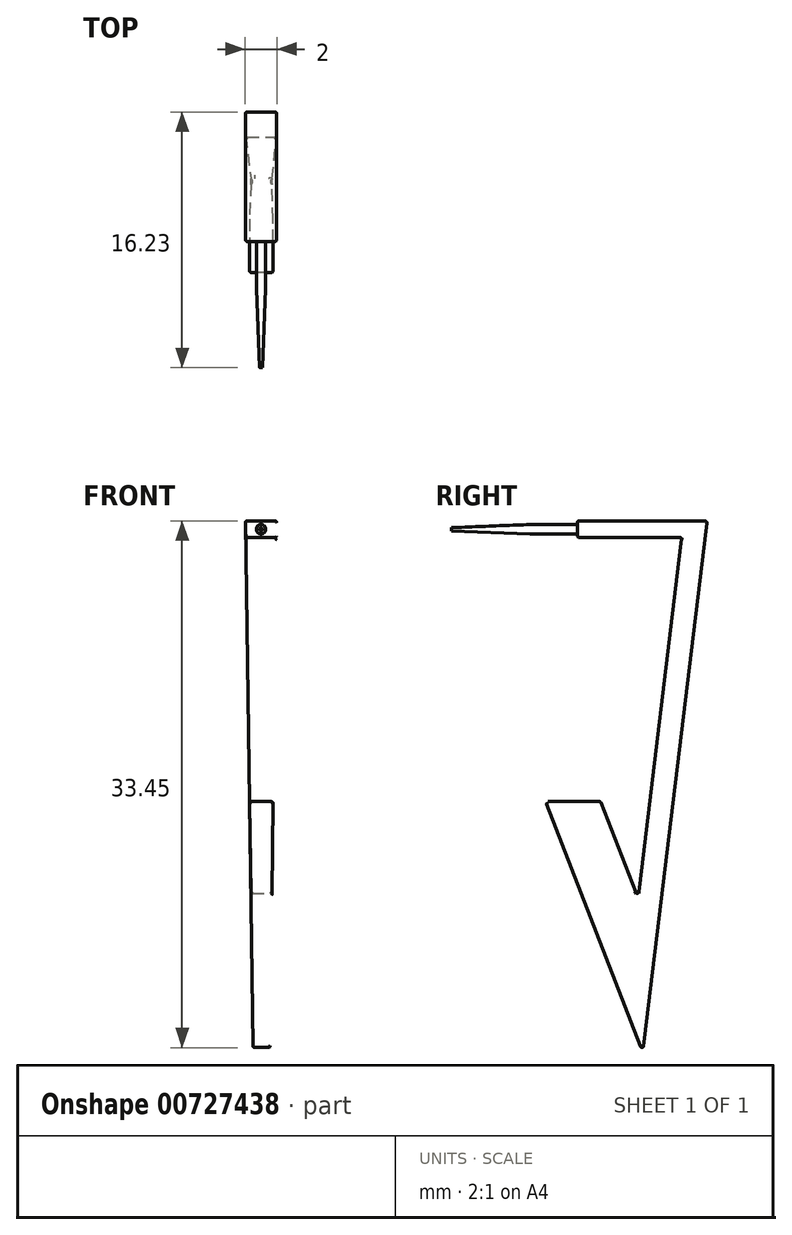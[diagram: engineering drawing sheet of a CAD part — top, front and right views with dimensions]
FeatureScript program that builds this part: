
annotation { "Feature Type Name" : "Feature", "Feature Type Description" : "" }
export const myFeature = defineFeature(function(context is Context, id is Id, definition is map)
    precondition{}
    {
        {
            var Q0;
            Q0=qCreatedBy(makeId("Right.planeOp"),FACE);
            var sketch = newSketch(context, id + "F0", { "sketchPlane" : qUnion([Q0])});
            skLineSegment(sketch, "E0", {"start": v(-6.63, 24.69) * mm, "end": v(1.6, 24.69) * mm});
            skLineSegment(sketch, "E1", {"start": v(1.6, 24.69) * mm, "end": v(-2.47, -9.07) * mm});
            skLineSegment(sketch, "E2", {"start": v(-2.47, -9.07) * mm, "end": v(-8.65, 6.86) * mm});
            skLineSegment(sketch, "E3", {"start": v(-8.65, 6.86) * mm, "end": v(-5.15, 6.86) * mm});
            skLineSegment(sketch, "E4", {"start": v(-5.15, 6.86) * mm, "end": v(-2.77, 0.73) * mm});
            skLineSegment(sketch, "E5", {"start": v(-2.77, 0.73) * mm, "end": v(0, 23.65) * mm});
            skLineSegment(sketch, "E6", {"start": v(0, 23.65) * mm, "end": v(-6.63, 23.65) * mm});
            skLineSegment(sketch, "E7", {"start": v(-6.63, 23.65) * mm, "end": v(-6.63, 24.69) * mm});
            skSolve(sketch);
        }
        {
            var Q0;
            Q0 = qSketchRegion(id + "F0", true);
            extrude(context, id + "F1", {"entities" : qUnion([Q0]), "endBound" : BoundingType.SYMMETRIC, "depth" : 2 * mm, "offsetDistance" : 25 * mm});
        }
        {
            var Q0;
            Q0=makeQuery(id+"F1.opExtrude","SWEPT_FACE",FACE,{"disambiguationData":[OSD([sQuery(id+"F0.wireOp",EDGE,"E1")])]});
            var sketch = newSketch(context, id + "F2", { "sketchPlane" : qUnion([Q0])});
            skLineSegment(sketch, "E8", {"start": v(-1, 24.7) * mm, "end": v(-0.55, -11.46) * mm});
            skLineSegment(sketch, "E9", {"start": v(-0.55, -11.46) * mm, "end": v(0.47, -11.46) * mm});
            skLineSegment(sketch, "E10", {"start": v(0.47, -11.46) * mm, "end": v(1, 24.7) * mm});
            skLineSegment(sketch, "E11", {"start": v(1, 24.7) * mm, "end": v(7.04, 24.06) * mm});
            skLineSegment(sketch, "E12", {"start": v(7.04, 24.06) * mm, "end": v(7.04, -14.41) * mm});
            skLineSegment(sketch, "E13", {"start": v(7.04, -14.41) * mm, "end": v(-7.18, -14.41) * mm});
            skLineSegment(sketch, "E14", {"start": v(-7.18, -14.41) * mm, "end": v(-8.07, 24.7) * mm});
            skLineSegment(sketch, "E15", {"start": v(-8.07, 24.7) * mm, "end": v(-1, 24.7) * mm});
            skSolve(sketch);
        }
        {
            var Q0;
            Q0 = qSketchRegion(id + "F2", true);
            extrude(context, id + "F3", {"entities" : qUnion([Q0]), "operationType" : NewBodyOperationType.REMOVE, "endBound" : BoundingType.SYMMETRIC, "oppositeDirection" : true, "depth" : 25 * mm, "offsetDistance" : 25 * mm});
        }
        {
            var Q0;
            Q0=makeQuery(id+"F1.opExtrude","SWEPT_FACE",FACE,{"disambiguationData":[OSD([sQuery(id+"F0.wireOp",EDGE,"E7")])]});
            var sketch = newSketch(context, id + "F4", { "sketchPlane" : qUnion([Q0])});
            skCircle(sketch, "E16", {"center": v(0, 24.17) * mm, "radius": 0.3 * mm});
            skPoint(sketch, "E16.centerSnap0", {"position": v(0.98, 24.17) * mm});
            skPoint(sketch, "E16.centerSnap1", {"position": v(0, 24.69) * mm});
            skSolve(sketch);
        }
        {
            var Q0;
            Q0 = qSketchRegion(id + "F4", true);
            extrude(context, id + "F5", {"entities" : qUnion([Q0]), "operationType" : NewBodyOperationType.ADD, "depth" : 8 * mm, "offsetDistance" : 25 * mm});
        }
        {
            var Q0;
            Q0=makeQuery(id+"F5.opExtrude","CAP_EDGE",EDGE,{"disambiguationData":[OSD([sQuery(id+"F4.wireOp",EDGE,"E16")])],"isStart":false});
            chamfer(context, id + "F6", {"entities" : qUnion([Q0]), "chamferType" : ChamferType.TWO_OFFSETS, "width1" : .2 * mm, "oppositeDirection" : false, "width2" : 5 * mm, "tangentPropagation" : true});
        }
        {
            var Q0;
            Q0=makeQuery(id+"F3.boolean.opBoolean","INTERSECT",EDGE,{"derivedFrom":[makeQuery(id+"F1.opExtrude","SWEPT_FACE",FACE,{"disambiguationData":[OSD([sQuery(id+"F0.wireOp",EDGE,"E4")])]}),makeQuery(id+"F3.opExtrude","SWEPT_FACE",FACE,{"disambiguationData":[OSD([sQuery(id+"F2.wireOp",EDGE,"E8")])]})]});
            var Q1;
            Q1=makeQuery(id+"F3.boolean.opBoolean","INTERSECT",EDGE,{"derivedFrom":[makeQuery(id+"F1.opExtrude","SWEPT_FACE",FACE,{"disambiguationData":[OSD([sQuery(id+"F0.wireOp",EDGE,"E0")])]}),makeQuery(id+"F3.opExtrude","SWEPT_FACE",FACE,{"disambiguationData":[OSD([sQuery(id+"F2.wireOp",EDGE,"E10")])]})]});
            var Q2;
            Q2=makeQuery(id+"F3.boolean.opBoolean","INTERSECT",EDGE,{"derivedFrom":[makeQuery(id+"F1.opExtrude","SWEPT_FACE",FACE,{"disambiguationData":[OSD([sQuery(id+"F0.wireOp",EDGE,"E5")])]}),makeQuery(id+"F3.opExtrude","SWEPT_FACE",FACE,{"disambiguationData":[OSD([sQuery(id+"F2.wireOp",EDGE,"E10")])]})]});
            var Q3;
            Q3=makeQuery(id+"F3.boolean.opBoolean","INTERSECT",EDGE,{"derivedFrom":[makeQuery(id+"F1.opExtrude","SWEPT_FACE",FACE,{"disambiguationData":[OSD([sQuery(id+"F0.wireOp",EDGE,"E3")])]}),makeQuery(id+"F3.opExtrude","SWEPT_FACE",FACE,{"disambiguationData":[OSD([sQuery(id+"F2.wireOp",EDGE,"E8")])]})]});
            var Q4;
            Q4=makeQuery(id+"F3.boolean.opBoolean","INTERSECT",EDGE,{"derivedFrom":[makeQuery(id+"F1.opExtrude","SWEPT_FACE",FACE,{"disambiguationData":[OSD([sQuery(id+"F0.wireOp",EDGE,"E0")])]}),makeQuery(id+"F3.opExtrude","SWEPT_FACE",FACE,{"disambiguationData":[OSD([sQuery(id+"F2.wireOp",EDGE,"E8")])]})]});
            var Q5;
            Q5=makeQuery(id+"F3.boolean.opBoolean","INTERSECT",EDGE,{"derivedFrom":[makeQuery(id+"F1.opExtrude","SWEPT_FACE",FACE,{"disambiguationData":[OSD([sQuery(id+"F0.wireOp",EDGE,"E2")])]}),makeQuery(id+"F3.opExtrude","SWEPT_FACE",FACE,{"disambiguationData":[OSD([sQuery(id+"F2.wireOp",EDGE,"E10")])]})]});
            var Q6;
            Q6=makeQuery(id+"F3.boolean.opBoolean","INTERSECT",EDGE,{"derivedFrom":[makeQuery(id+"F1.opExtrude","SWEPT_FACE",FACE,{"disambiguationData":[OSD([sQuery(id+"F0.wireOp",EDGE,"E5")])]}),makeQuery(id+"F3.opExtrude","SWEPT_FACE",FACE,{"disambiguationData":[OSD([sQuery(id+"F2.wireOp",EDGE,"E8")])]})]});
            var Q7;
            Q7=makeQuery(id+"F3.boolean.opBoolean","INTERSECT",EDGE,{"derivedFrom":[makeQuery(id+"F1.opExtrude","SWEPT_FACE",FACE,{"disambiguationData":[OSD([sQuery(id+"F0.wireOp",EDGE,"E6")])]}),makeQuery(id+"F3.opExtrude","SWEPT_FACE",FACE,{"disambiguationData":[OSD([sQuery(id+"F2.wireOp",EDGE,"E8")])]})]});
            var Q8;
            Q8=makeQuery(id+"F3.boolean.opBoolean","INTERSECT",EDGE,{"derivedFrom":[makeQuery(id+"F1.opExtrude","SWEPT_FACE",FACE,{"disambiguationData":[OSD([sQuery(id+"F0.wireOp",EDGE,"E2")])]}),makeQuery(id+"F3.opExtrude","SWEPT_FACE",FACE,{"disambiguationData":[OSD([sQuery(id+"F2.wireOp",EDGE,"E8")])]})]});
            var Q9;
            Q9=makeQuery(id+"F3.boolean.opBoolean","INTERSECT",EDGE,{"derivedFrom":[makeQuery(id+"F1.opExtrude","SWEPT_FACE",FACE,{"disambiguationData":[OSD([sQuery(id+"F0.wireOp",EDGE,"E1")])]}),makeQuery(id+"F3.opExtrude","SWEPT_FACE",FACE,{"disambiguationData":[OSD([sQuery(id+"F2.wireOp",EDGE,"E8")])]})]});
            var Q10;
            Q10=makeQuery(id+"F3.boolean.opBoolean","INTERSECT",EDGE,{"derivedFrom":[makeQuery(id+"F1.opExtrude","SWEPT_FACE",FACE,{"disambiguationData":[OSD([sQuery(id+"F0.wireOp",EDGE,"E3")])]}),makeQuery(id+"F3.opExtrude","SWEPT_FACE",FACE,{"disambiguationData":[OSD([sQuery(id+"F2.wireOp",EDGE,"E10")])]})]});
            var Q11;
            Q11=makeQuery(id+"F1.opExtrude","SWEPT_EDGE",EDGE,{"disambiguationData":[OSD([sQuery(id+"F0.wireOp",EDGE,"E0"),sQuery(id+"F0.wireOp",EDGE,"E1")])]});
            var Q12;
            {var subQ0=sQuery(id+"F4.wireOp",EDGE,"E16");Q12=makeQuery(id+"F6.opChamfer","BLEND_EDGE",EDGE,{"blendedFrom":[makeQuery(id+"F5.opExtrude","CAP_EDGE",EDGE,{"disambiguationData":[OSD([subQ0])],"isStart":false}),makeQuery(id+"F5.opExtrude","SWEPT_FACE",FACE,{"disambiguationData":[OSD([subQ0])]})],"blendedInto":[makeQuery(id+"F5.opExtrude","SWEPT_FACE",FACE,{"disambiguationData":[OSD([subQ0])]})]});}
            var Q13;
            Q13=makeQuery(id+"F3.boolean.opBoolean","INTERSECT",EDGE,{"derivedFrom":[makeQuery(id+"F1.opExtrude","SWEPT_FACE",FACE,{"disambiguationData":[OSD([sQuery(id+"F0.wireOp",EDGE,"E1")])]}),makeQuery(id+"F3.opExtrude","SWEPT_FACE",FACE,{"disambiguationData":[OSD([sQuery(id+"F2.wireOp",EDGE,"E10")])]})]});
            var Q14;
            Q14=makeQuery(id+"F3.boolean.opBoolean","INTERSECT",EDGE,{"derivedFrom":[makeQuery(id+"F1.opExtrude","SWEPT_FACE",FACE,{"disambiguationData":[OSD([sQuery(id+"F0.wireOp",EDGE,"E4")])]}),makeQuery(id+"F3.opExtrude","SWEPT_FACE",FACE,{"disambiguationData":[OSD([sQuery(id+"F2.wireOp",EDGE,"E10")])]})]});
            var Q15;
            Q15=makeQuery(id+"F1.opExtrude","SWEPT_EDGE",EDGE,{"disambiguationData":[OSD([sQuery(id+"F0.wireOp",EDGE,"E6"),sQuery(id+"F0.wireOp",EDGE,"E7")])]});
            var Q16;
            Q16=makeQuery(id+"F3.boolean.opBoolean","INTERSECT",EDGE,{"derivedFrom":[makeQuery(id+"F1.opExtrude","SWEPT_FACE",FACE,{"disambiguationData":[OSD([sQuery(id+"F0.wireOp",EDGE,"E7")])]}),makeQuery(id+"F3.opExtrude","SWEPT_FACE",FACE,{"disambiguationData":[OSD([sQuery(id+"F2.wireOp",EDGE,"E8")])]})]});
            var Q17;
            Q17=makeQuery(id+"F1.opExtrude","SWEPT_EDGE",EDGE,{"disambiguationData":[OSD([sQuery(id+"F0.wireOp",EDGE,"E5"),sQuery(id+"F0.wireOp",EDGE,"E6")])]});
            var Q18;
            Q18=makeQuery(id+"F1.opExtrude","SWEPT_EDGE",EDGE,{"disambiguationData":[OSD([sQuery(id+"F0.wireOp",EDGE,"E4"),sQuery(id+"F0.wireOp",EDGE,"E5")])]});
            var Q19;
            Q19=makeQuery(id+"F3.boolean.opBoolean","INTERSECT",EDGE,{"derivedFrom":[makeQuery(id+"F1.opExtrude","SWEPT_FACE",FACE,{"disambiguationData":[OSD([sQuery(id+"F0.wireOp",EDGE,"E7")])]}),makeQuery(id+"F3.opExtrude","SWEPT_FACE",FACE,{"disambiguationData":[OSD([sQuery(id+"F2.wireOp",EDGE,"E10")])]})]});
            var Q20;
            Q20=makeQuery(id+"F1.opExtrude","SWEPT_EDGE",EDGE,{"disambiguationData":[OSD([sQuery(id+"F0.wireOp",EDGE,"E2"),sQuery(id+"F0.wireOp",EDGE,"E3")])]});
            var Q21;
            Q21=makeQuery(id+"F1.opExtrude","SWEPT_EDGE",EDGE,{"disambiguationData":[OSD([sQuery(id+"F0.wireOp",EDGE,"E1"),sQuery(id+"F0.wireOp",EDGE,"E2")])]});
            var Q22;
            Q22=makeQuery(id+"F1.opExtrude","SWEPT_EDGE",EDGE,{"disambiguationData":[OSD([sQuery(id+"F0.wireOp",EDGE,"E3"),sQuery(id+"F0.wireOp",EDGE,"E4")])]});
            var Q23;
            Q23=makeQuery(id+"F1.opExtrude","SWEPT_EDGE",EDGE,{"disambiguationData":[OSD([sQuery(id+"F0.wireOp",EDGE,"E0"),sQuery(id+"F0.wireOp",EDGE,"E7")])]});
            var Q24;
            Q24=makeQuery(id+"F3.boolean.opBoolean","INTERSECT",EDGE,{"derivedFrom":[makeQuery(id+"F1.opExtrude","SWEPT_FACE",FACE,{"disambiguationData":[OSD([sQuery(id+"F0.wireOp",EDGE,"E6")])]}),makeQuery(id+"F3.opExtrude","SWEPT_FACE",FACE,{"disambiguationData":[OSD([sQuery(id+"F2.wireOp",EDGE,"E10")])]})]});
            fillet(context, id + "F7", {"entities" : qUnion([Q0, Q1, Q2, Q3, Q4, Q5, Q6, Q7, Q8, Q9, Q10, Q11, Q12, Q13, Q14, Q15, Q16, Q17, Q18, Q19, Q20, Q21, Q22, Q23, Q24]), "radius" : .1 * mm, "tangentPropagation" : true, "allowEdgeOverflow" : false});
        }
    });
